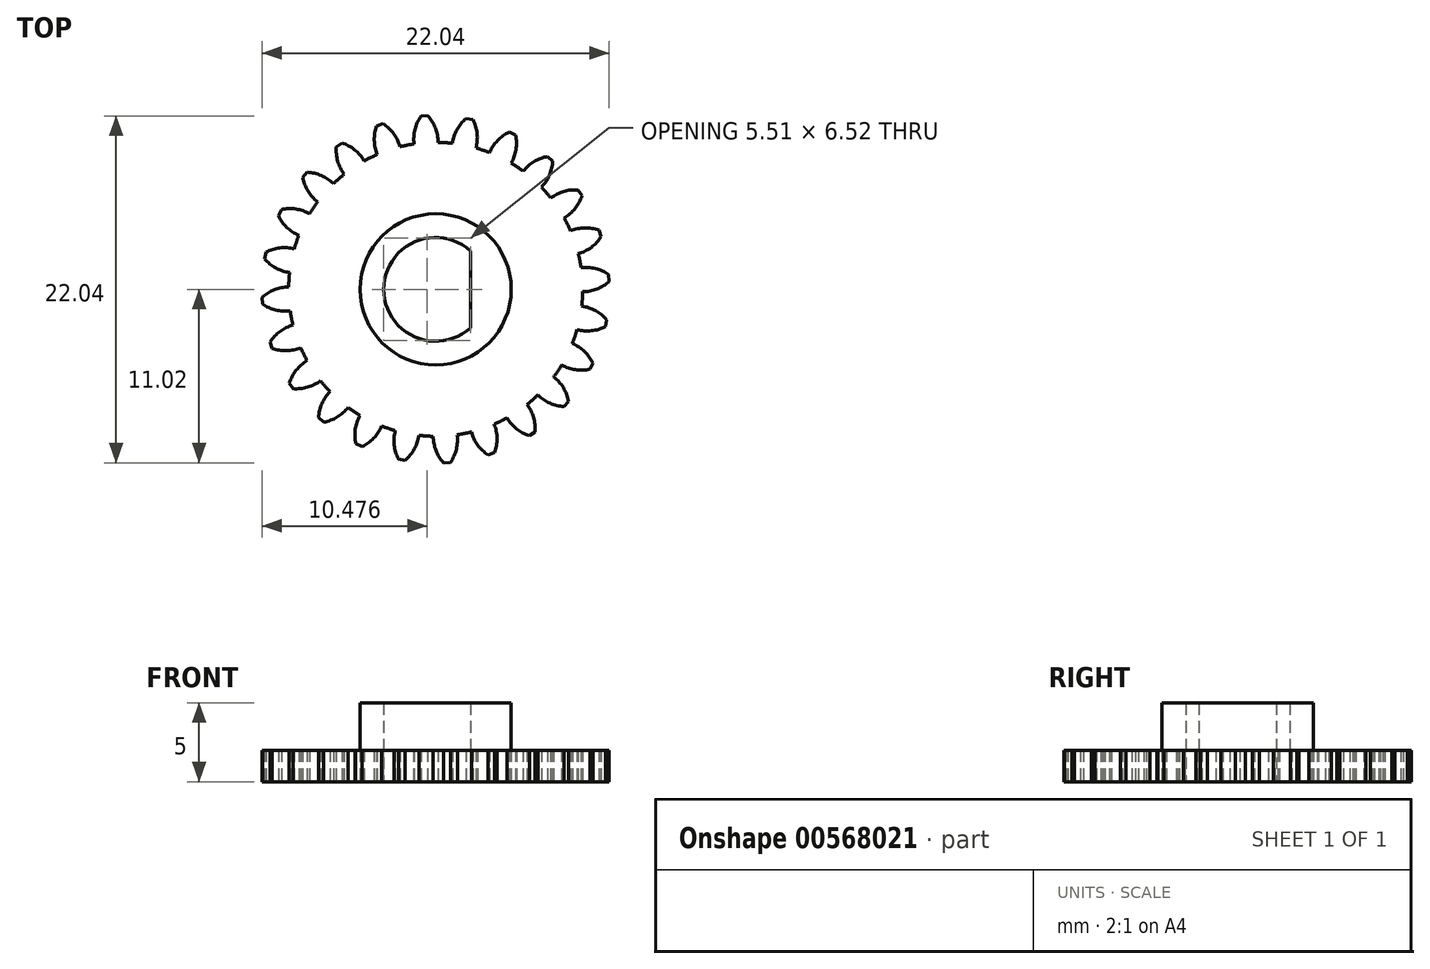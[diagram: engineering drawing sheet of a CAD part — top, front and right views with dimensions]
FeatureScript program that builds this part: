
annotation { "Feature Type Name" : "Feature", "Feature Type Description" : "" }
export const myFeature = defineFeature(function(context is Context, id is Id, definition is map)
    precondition{}
    {
        {
            var Q0;
            Q0=qCreatedBy(makeId("Top.planeOp"),FACE);
            var sketch = newSketch(context, id + "F0", { "sketchPlane" : qUnion([Q0])});
            skCircle(sketch, "E0", {"center": v(0, 0) * mm, "radius": 9.34 * mm});
            skCircle(sketch, "E1", {"center": v(0, 0) * mm, "radius": 10.19 * mm, "construction": true});
            skCircle(sketch, "E2", {"center": v(0, 0) * mm, "radius": 11.03 * mm, "construction": true});
            skLineSegment(sketch, "E3", {"start": v(0, 0) * mm, "end": v(-1.07, 16.4) * mm, "construction": true});
            skLineSegment(sketch, "E4", {"start": v(0, 10.19) * mm, "end": v(-11.74, 10.19) * mm, "construction": true});
            skLineSegment(sketch, "E5", {"start": v(0, 10.19) * mm, "end": v(-8.82, 6.98) * mm, "construction": true});
            skCircle(sketch, "E6", {"center": v(0, 10.19) * mm, "radius": 2.54 * mm, "construction": true});
            skCircle(sketch, "E7", {"center": v(-2.4, 9.32) * mm, "radius": 2.54 * mm, "construction": true});
            skArc(sketch, "E8", {"start": v(0.15, 9.34) * mm, "mid": v(-0.02, 10.24) * mm, "end": v(-0.5, 11.02) * mm});
            skArc(sketch, "E9.MirrorCS", {"start": v(-1.37, 9.24) * mm, "mid": v(-1.32, 10.15) * mm, "end": v(-0.94, 11) * mm});
            skLineSegment(sketch, "E10", {"start": v(-0.94, 11) * mm, "end": v(-0.5, 11.02) * mm});
            skArc(sketch, "E11", {"start": v(2.21, 2.45) * mm, "mid": v(-3.3, 0) * mm, "end": v(2.21, -2.45) * mm});
            skCircle(sketch, "E12", {"center": v(0, 0) * mm, "radius": 4.8 * mm});
            skLineSegment(sketch, "E13", {"start": v(2.21, 2.45) * mm, "end": v(2.21, -2.45) * mm});
            skSolve(sketch);
        }
        {
            var Q0;
            {var subQ0=sQuery(id+"F0.wireOp",EDGE,"3a9ebfa4-2dc7-4d1a-8901-d56b49148436");var subQ1=makeQuery(id+"F0.imprint","INTERSECT",VERTEX,{"derivedFrom":[subQ0,sQuery(id+"F0.wireOp",EDGE,"RVtRNbwh-xyOM-P5Wh-Gehi-Ms3fEEbLKqf4")]});Q0=makeQuery(id+"F0.imprint","IMPRINT",FACE,{"disambiguationData":[TD([[makeQuery(id+"F0.imprint","IMPRINT",EDGE,{"disambiguationData":[TD([[subQ1,-1.0]])],"derivedFrom":subQ0}),1.0]])]});}
            var Q1;
            {var subQ0=sQuery(id+"F0.wireOp",EDGE,"E0");var subQ1=makeQuery(id+"F0.imprint","INTERSECT",VERTEX,{"derivedFrom":[subQ0,sQuery(id+"F0.wireOp",EDGE,"E8")]});Q1=makeQuery(id+"F0.imprint","IMPRINT",FACE,{"disambiguationData":[TD([[makeQuery(id+"F0.imprint","IMPRINT",EDGE,{"disambiguationData":[TD([[subQ1,-1.0]])],"derivedFrom":subQ0}),1.0]])]});}
            var Q2;
            Q2=makeQuery(id+"F0.imprint","IMPRINT",FACE,{"disambiguationData":[TD([[makeQuery(id+"F0.imprint","IMPRINT",EDGE,{"derivedFrom":sQuery(id+"F0.wireOp",EDGE,"E11")}),-1.0]])]});
            extrude(context, id + "F1", {"entities" : qUnion([Q0, Q1, Q2]), "depth" : 2 * mm, "offsetDistance" : 25 * mm});
        }
        {
            var Q0;
            {var subQ0=sQuery(id+"F0.wireOp",EDGE,"E8");Q0=makeQuery(id+"F0.imprint","IMPRINT",FACE,{"disambiguationData":[TD([[makeQuery(id+"F0.imprint","IMPRINT",EDGE,{"derivedFrom":subQ0}),1.0]])]});}
            extrude(context, id + "F2", {"entities" : qUnion([Q0]), "depth" : 2 * mm, "offsetDistance" : 25 * mm});
        }
        {
            var Q0;
            Q0=makeQuery(id+"F2.opExtrude","SWEPT_BODY",BODY,{"disambiguationData":[OSD([sQuery(id+"F0.wireOp",EDGE,"E0"),sQuery(id+"F0.wireOp",EDGE,"E8"),sQuery(id+"F0.wireOp",EDGE,"E9.MirrorCS"),sQuery(id+"F0.wireOp",EDGE,"E10")])]});
            var Q1;
            Q1=makeQuery(id+"F1.opExtrude","SWEPT_FACE",FACE,{"disambiguationData":[OSD([sQuery(id+"F0.wireOp",EDGE,"E0")])]});
            circularPattern(context, id + "F3", {"operationType" : NewBodyOperationType.ADD, "entities" : qUnion([Q0]), "axis" : qUnion([Q1]), "angle" : 360 * degree, "instanceCount" : 24, "equalSpace" : true});
        }
        {
            var Q0;
            Q0=makeQuery(id+"F0.imprint","IMPRINT",FACE,{"disambiguationData":[TD([[makeQuery(id+"F0.imprint","IMPRINT",EDGE,{"derivedFrom":sQuery(id+"F0.wireOp",EDGE,"E11")}),-1.0]])]});
            extrude(context, id + "F4", {"entities" : qUnion([Q0]), "operationType" : NewBodyOperationType.ADD, "depth" : 5 * mm, "offsetDistance" : 25 * mm});
        }
    });
